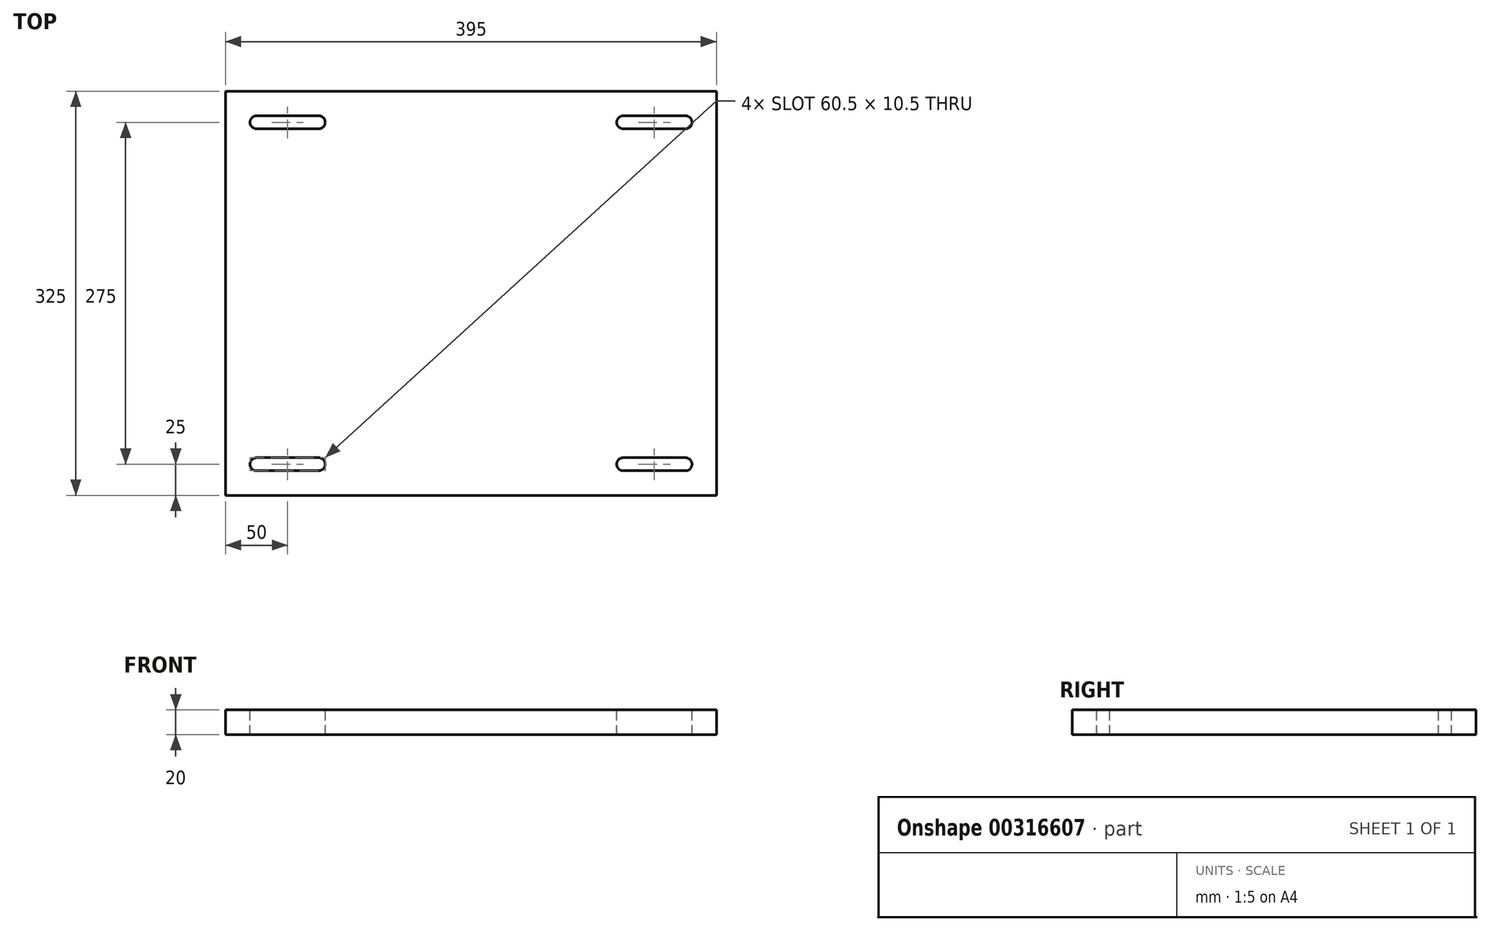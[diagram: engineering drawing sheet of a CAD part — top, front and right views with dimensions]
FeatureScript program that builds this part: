
annotation { "Feature Type Name" : "Feature", "Feature Type Description" : "" }
export const myFeature = defineFeature(function(context is Context, id is Id, definition is map)
    precondition{}
    {
        {
            var Q0;
            Q0=qCreatedBy(makeId("Top.planeOp"),FACE);
            var sketch = newSketch(context, id + "F0", { "sketchPlane" : qUnion([Q0])});
            skLineSegment(sketch, "E0.bottom", {"start": v(197.5, -162.5) * mm, "end": v(-197.5, -162.5) * mm});
            skLineSegment(sketch, "E0.top", {"start": v(197.5, 162.5) * mm, "end": v(-197.5, 162.5) * mm});
            skLineSegment(sketch, "E0.left", {"start": v(197.5, -162.5) * mm, "end": v(197.5, 162.5) * mm});
            skLineSegment(sketch, "E0.right", {"start": v(-197.5, -162.5) * mm, "end": v(-197.5, 162.5) * mm});
            skPoint(sketch, "E0.middle", {"position": v(0, 0) * mm});
            skSolve(sketch);
        }
        {
            var Q0;
            Q0=makeQuery(id+"F0.imprint","IMPRINT",FACE,{"disambiguationData":[TD([[makeQuery(id+"F0.imprint","IMPRINT",EDGE,{"derivedFrom":sQuery(id+"F0.wireOp",EDGE,"E0.bottom")}),-1.0]])]});
            extrude(context, id + "F1", {"entities" : qUnion([Q0]), "oppositeDirection" : true, "depth" : 20 * mm});
        }
        {
            var Q0;
            Q0=makeQuery(id+"F1.opExtrude","CAP_FACE",FACE,{"disambiguationData":[OSD([sQuery(id+"F0.wireOp",EDGE,"E0.bottom"),sQuery(id+"F0.wireOp",EDGE,"E0.top"),sQuery(id+"F0.wireOp",EDGE,"E0.left"),sQuery(id+"F0.wireOp",EDGE,"E0.right")])],"isStart":true});
            var sketch = newSketch(context, id + "F2", { "sketchPlane" : qUnion([Q0])});
            skLineSegment(sketch, "E1", {"start": v(0, -162.5) * mm, "end": v(0, -137.5) * mm, "construction": true});
            skPoint(sketch, "E1.endSnap0", {"position": v(0, -162.5) * mm});
            skLineSegment(sketch, "E2", {"start": v(0, -137.5) * mm, "end": v(-172.5, -137.5) * mm, "construction": true});
            skPoint(sketch, "E3", {"position": v(-172.5, -137.5) * mm});
            skPoint(sketch, "E4", {"position": v(-122.5, -137.5) * mm});
            skArc(sketch, "E5", {"start": v(-172.5, -132.25) * mm, "mid": v(-177.75, -137.5) * mm, "end": v(-172.5, -142.75) * mm});
            skArc(sketch, "E6", {"start": v(-122.5, -142.75) * mm, "mid": v(-117.25, -137.5) * mm, "end": v(-122.5, -132.25) * mm});
            skLineSegment(sketch, "E7", {"start": v(-172.5, -132.25) * mm, "end": v(-122.5, -132.25) * mm});
            skLineSegment(sketch, "E8", {"start": v(-172.5, -142.75) * mm, "end": v(-122.5, -142.75) * mm});
            skLineSegment(sketch, "E9.MirrorCS", {"start": v(172.5, -132.25) * mm, "end": v(122.5, -132.25) * mm});
            skArc(sketch, "E10.MirrorCS", {"start": v(172.5, -132.25) * mm, "mid": v(177.75, -137.5) * mm, "end": v(172.5, -142.75) * mm});
            skLineSegment(sketch, "E11.MirrorCS", {"start": v(172.5, -142.75) * mm, "end": v(122.5, -142.75) * mm});
            skArc(sketch, "E12.MirrorCS", {"start": v(122.5, -142.75) * mm, "mid": v(117.25, -137.5) * mm, "end": v(122.5, -132.25) * mm});
            skLineSegment(sketch, "E13.MirrorCS", {"start": v(-172.5, 132.25) * mm, "end": v(-122.5, 132.25) * mm});
            skArc(sketch, "E14.MirrorCS", {"start": v(-172.5, 132.25) * mm, "mid": v(-177.75, 137.5) * mm, "end": v(-172.5, 142.75) * mm});
            skLineSegment(sketch, "E15.MirrorCS", {"start": v(-172.5, 142.75) * mm, "end": v(-122.5, 142.75) * mm});
            skArc(sketch, "E16.MirrorCS", {"start": v(-122.5, 142.75) * mm, "mid": v(-117.25, 137.5) * mm, "end": v(-122.5, 132.25) * mm});
            skLineSegment(sketch, "E17.MirrorCS", {"start": v(172.5, 132.25) * mm, "end": v(122.5, 132.25) * mm});
            skArc(sketch, "E18.MirrorCS", {"start": v(122.5, 142.75) * mm, "mid": v(117.25, 137.5) * mm, "end": v(122.5, 132.25) * mm});
            skLineSegment(sketch, "E19.MirrorCS", {"start": v(172.5, 142.75) * mm, "end": v(122.5, 142.75) * mm});
            skArc(sketch, "E20.MirrorCS", {"start": v(172.5, 132.25) * mm, "mid": v(177.75, 137.5) * mm, "end": v(172.5, 142.75) * mm});
            skSolve(sketch);
        }
        {
            var Q0;
            Q0=makeQuery(id+"F2.imprint","IMPRINT",FACE,{"disambiguationData":[TD([[makeQuery(id+"F2.imprint","IMPRINT",EDGE,{"derivedFrom":sQuery(id+"F2.wireOp",EDGE,"E13.MirrorCS")}),1.0]])]});
            var Q1;
            Q1=makeQuery(id+"F2.imprint","IMPRINT",FACE,{"disambiguationData":[TD([[makeQuery(id+"F2.imprint","IMPRINT",EDGE,{"derivedFrom":sQuery(id+"F2.wireOp",EDGE,"E5")}),1.0]])]});
            var Q2;
            Q2=makeQuery(id+"F2.imprint","IMPRINT",FACE,{"disambiguationData":[TD([[makeQuery(id+"F2.imprint","IMPRINT",EDGE,{"derivedFrom":sQuery(id+"F2.wireOp",EDGE,"E9.MirrorCS")}),1.0]])]});
            var Q3;
            Q3=makeQuery(id+"F2.imprint","IMPRINT",FACE,{"disambiguationData":[TD([[makeQuery(id+"F2.imprint","IMPRINT",EDGE,{"derivedFrom":sQuery(id+"F2.wireOp",EDGE,"E17.MirrorCS")}),-1.0]])]});
            extrude(context, id + "F3", {"entities" : qUnion([Q0, Q1, Q2, Q3]), "operationType" : NewBodyOperationType.REMOVE, "oppositeDirection" : true, "depth" : 25 * mm});
        }
    });
